# Revit family: Dock-Shelter_Perma-Tech_PS-40-Ground-Level
name_source: partatom
category: Generic Models
units: mm (PartAtom-declared; Revit-internal decimal feet)

## family parameters
Always vertical = Yes
Can host rebar = No
Cut with Voids When Loaded = Yes
Host = Wall
Maintain Annotation Orientation = No
Part Type = Normal
Room Calculation Point = No
Round Connector Dimension = Use Diameter
Shared = No

## types (1)
- PS-40 Ground Lvl
    Arcat Spec = https://www.arcat.com
    Ballards Height = 30"
    Bottom Proj. = 9"
    Cost = 0 $
    Cover = Cover Black
    Curtain Drop = 23"
    Default Elevation = 0"
    Head Curtain Proj. = 9"
    Manufacturer = Perma Tech Inc.
    Model = Rigid Ground Shelter
    Opening Height = 84"
    Opening Width = 51"
    Product Documentation Link = https://www.permatechinc.com
    Product Info = https://www.arcat.com
    Product Page URL = https://www.permatechinc.com
    Side Curtain Width = 12"
    Side Pad Width = 3"
    Specification = https://www.permatechinc.com
    Top Proj. = 9"
    URL = https://www.permatechinc.com
    Unit Height = 90"
    Unit Width = 55"

## geometry (parser evidence)
native form markers: Sweep x4
no freeform markers — native parametric forms only
